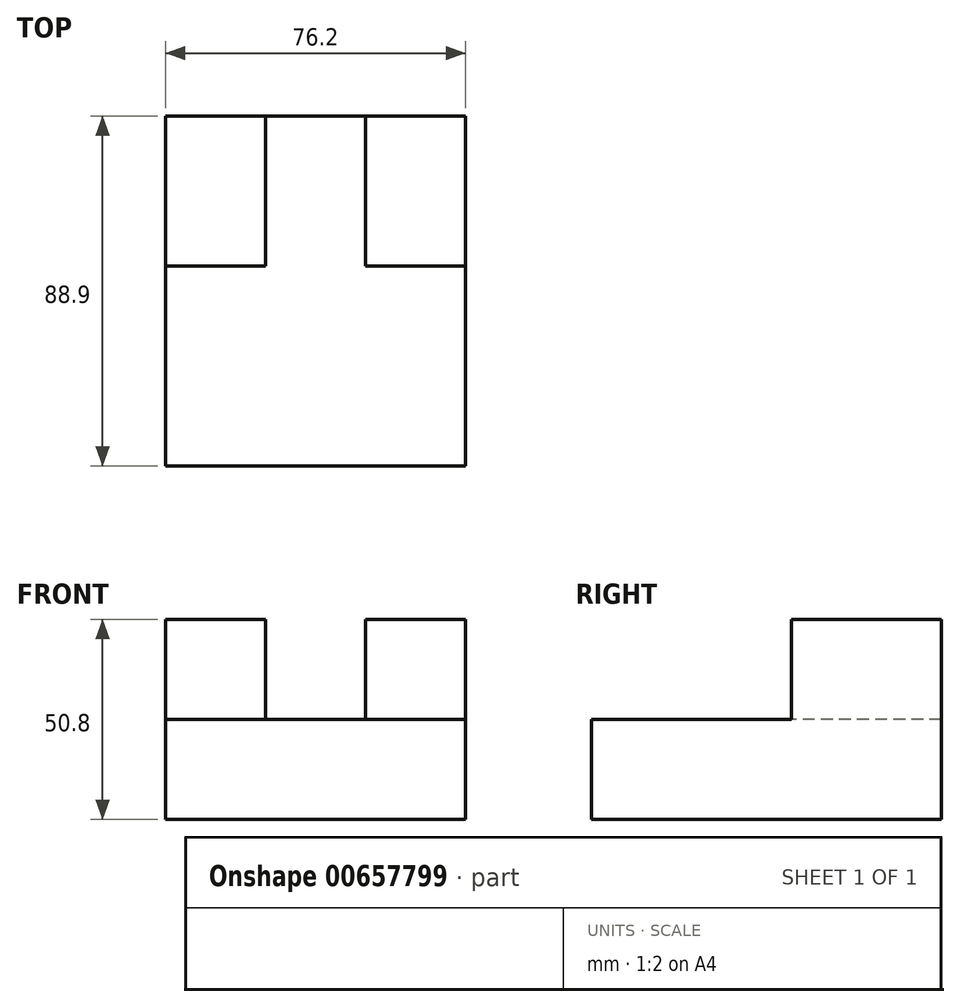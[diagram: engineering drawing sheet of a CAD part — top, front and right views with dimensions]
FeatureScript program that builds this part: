
annotation { "Feature Type Name" : "Feature", "Feature Type Description" : "" }
export const myFeature = defineFeature(function(context is Context, id is Id, definition is map)
    precondition{}
    {
        {
            var Q0;
            Q0=qCreatedBy(makeId("Top.planeOp"),FACE);
            var sketch = newSketch(context, id + "F0", { "sketchPlane" : qUnion([Q0])});
            skLineSegment(sketch, "E0.bottom", {"start": v(-80.92, 99.11) * mm, "end": v(-4.72, 99.11) * mm});
            skLineSegment(sketch, "E0.top", {"start": v(-80.92, 10.21) * mm, "end": v(-4.72, 10.21) * mm});
            skLineSegment(sketch, "E0.left", {"start": v(-80.92, 99.11) * mm, "end": v(-80.92, 10.21) * mm});
            skLineSegment(sketch, "E0.right", {"start": v(-4.72, 99.11) * mm, "end": v(-4.72, 10.21) * mm});
            skSolve(sketch);
        }
        {
            var Q0;
            Q0 = qSketchRegion(id + "F0", true);
            extrude(context, id + "F1", {"entities" : qUnion([Q0]), "depth" : 25.4 * mm, "offsetDistance" : 25.4 * mm});
        }
        {
            var Q0;
            Q0=makeQuery(id+"F1.opExtrude","CAP_FACE",FACE,{"disambiguationData":[OSD([sQuery(id+"F0.wireOp",EDGE,"E0.bottom"),sQuery(id+"F0.wireOp",EDGE,"E0.top"),sQuery(id+"F0.wireOp",EDGE,"E0.left"),sQuery(id+"F0.wireOp",EDGE,"E0.right")])],"isStart":false});
            var sketch = newSketch(context, id + "F2", { "sketchPlane" : qUnion([Q0])});
            skLineSegment(sketch, "E1.bottom", {"start": v(-80.92, 99.11) * mm, "end": v(-55.52, 99.11) * mm});
            skLineSegment(sketch, "E1.top", {"start": v(-80.92, 61.01) * mm, "end": v(-55.52, 61.01) * mm});
            skLineSegment(sketch, "E1.left", {"start": v(-80.92, 99.11) * mm, "end": v(-80.92, 61.01) * mm});
            skLineSegment(sketch, "E1.right", {"start": v(-55.52, 99.11) * mm, "end": v(-55.52, 61.01) * mm});
            skSolve(sketch);
        }
        {
            var Q0;
            Q0 = qSketchRegion(id + "F2", true);
            extrude(context, id + "F3", {"entities" : qUnion([Q0]), "operationType" : NewBodyOperationType.ADD, "depth" : 25.4 * mm, "offsetDistance" : 25.4 * mm});
        }
        {
            var Q0;
            Q0=makeQuery(id+"F1.opExtrude","CAP_FACE",FACE,{"disambiguationData":[OSD([sQuery(id+"F0.wireOp",EDGE,"E0.bottom"),sQuery(id+"F0.wireOp",EDGE,"E0.top"),sQuery(id+"F0.wireOp",EDGE,"E0.left"),sQuery(id+"F0.wireOp",EDGE,"E0.right")])],"isStart":false});
            var sketch = newSketch(context, id + "F4", { "sketchPlane" : qUnion([Q0])});
            skPoint(sketch, "E2.oppositeSnap0", {"position": v(-30.12, 99.11) * mm});
            skLineSegment(sketch, "E2.bottom", {"start": v(-4.72, 99.11) * mm, "end": v(-30.12, 99.11) * mm});
            skLineSegment(sketch, "E2.top", {"start": v(-4.72, 61.01) * mm, "end": v(-30.12, 61.01) * mm});
            skLineSegment(sketch, "E2.left", {"start": v(-4.72, 99.11) * mm, "end": v(-4.72, 61.01) * mm});
            skLineSegment(sketch, "E2.right", {"start": v(-30.12, 99.11) * mm, "end": v(-30.12, 61.01) * mm});
            skSolve(sketch);
        }
        {
            var Q0;
            Q0 = qSketchRegion(id + "F4", true);
            extrude(context, id + "F5", {"entities" : qUnion([Q0]), "operationType" : NewBodyOperationType.ADD, "depth" : 25.4 * mm, "offsetDistance" : 25.4 * mm});
        }
    });
